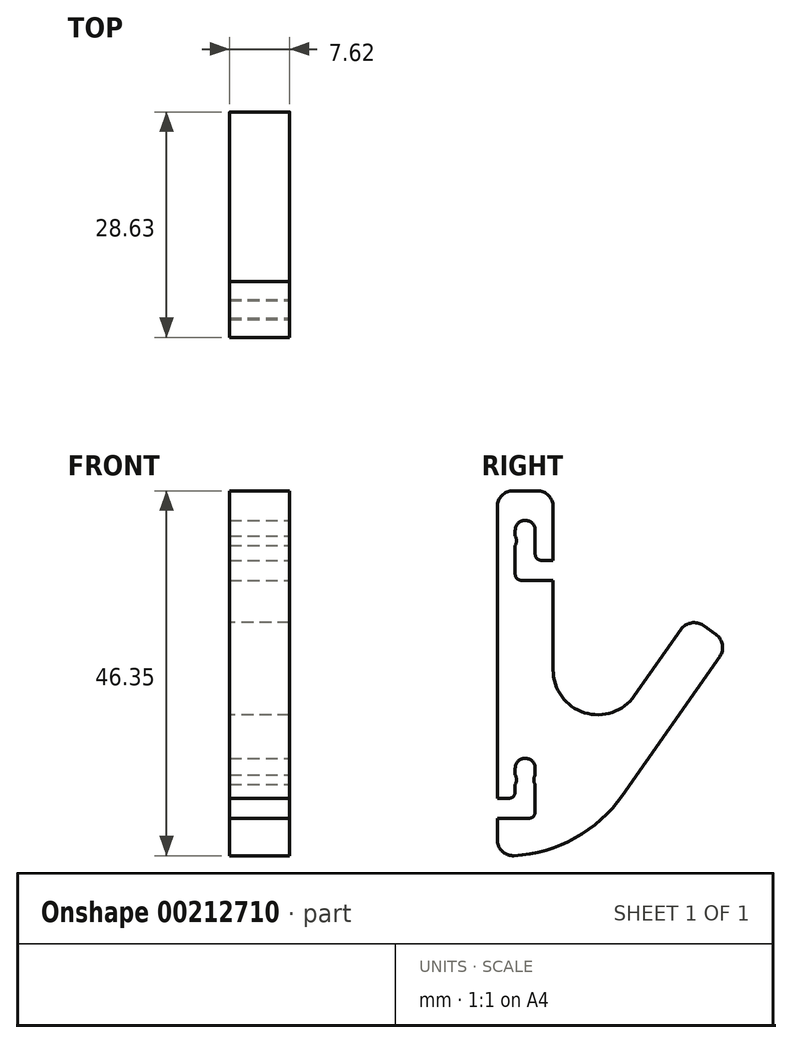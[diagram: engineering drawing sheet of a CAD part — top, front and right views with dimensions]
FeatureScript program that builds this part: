
annotation { "Feature Type Name" : "Feature", "Feature Type Description" : "" }
export const myFeature = defineFeature(function(context is Context, id is Id, definition is map)
    precondition{}
    {
        {
            var Q0;
            Q0=qCreatedBy(makeId("Right.planeOp"),FACE);
            var sketch = newSketch(context, id + "F0", { "sketchPlane" : qUnion([Q0])});
            skLineSegment(sketch, "E0", {"start": v(0, 0) * mm, "end": v(0, 42.36) * mm});
            skLineSegment(sketch, "E1", {"start": v(0, 42.36) * mm, "end": v(7.1, 42.36) * mm});
            skLineSegment(sketch, "E2", {"start": v(7.1, 42.36) * mm, "end": v(7.1, 19.6) * mm});
            skLineSegment(sketch, "E3", {"start": v(29.42, 22.97) * mm, "end": v(24.5, 26.4) * mm});
            skArc(sketch, "E4", {"start": v(7.1, 19.6) * mm, "mid": v(11.08, 14.17) * mm, "end": v(17.45, 16.33) * mm});
            skLineSegment(sketch, "E5", {"start": v(24.5, 26.4) * mm, "end": v(17.45, 16.33) * mm});
            skArc(sketch, "E6", {"start": v(0, -3.98) * mm, "mid": v(8.95, -2.25) * mm, "end": v(15.9, 3.65) * mm});
            skLineSegment(sketch, "E7", {"start": v(29.42, 22.97) * mm, "end": v(15.9, 3.65) * mm});
            skLineSegment(sketch, "E8", {"start": v(0, 0) * mm, "end": v(0, -3.98) * mm});
            skSolve(sketch);
        }
        {
            var Q0;
            Q0=makeQuery(id+"F0.imprint","IMPRINT",FACE,{"disambiguationData":[TD([[makeQuery(id+"F0.imprint","IMPRINT",EDGE,{"derivedFrom":sQuery(id+"F0.wireOp",EDGE,"E0")}),-1.0]])]});
            extrude(context, id + "F1", {"entities" : qUnion([Q0]), "depth" : 7.62 * mm, "symmetric" : true});
        }
        {
            var Q0;
            Q0=makeQuery(id+"F1.opExtrude","SWEPT_EDGE",EDGE,{"disambiguationData":[OSD([sQuery(id+"F0.wireOp",EDGE,"E1"),sQuery(id+"F0.wireOp",EDGE,"E2")])]});
            var Q1;
            Q1=makeQuery(id+"F1.opExtrude","SWEPT_EDGE",EDGE,{"disambiguationData":[OSD([sQuery(id+"F0.wireOp",EDGE,"do6iOSd0-p59h-Iph2-EZYE-FqhHj6ALnol1"),sQuery(id+"F0.wireOp",EDGE,"T0NzOJQf-1ohU-N6pa-0O5Z-Gt8aX7xeZM4e")])]});
            var Q2;
            Q2=makeQuery(id+"F1.opExtrude","SWEPT_EDGE",EDGE,{"disambiguationData":[OSD([sQuery(id+"F0.wireOp",EDGE,"do6iOSd0-p59h-Iph2-EZYE-FqhHj6ALnol1"),sQuery(id+"F0.wireOp",EDGE,"E4")])]});
            var Q3;
            Q3=makeQuery(id+"F1.opExtrude","SWEPT_EDGE",EDGE,{"disambiguationData":[OSD([sQuery(id+"F0.wireOp",EDGE,"do6iOSd0-p59h-Iph2-EZYE-FqhHj6ALnol1"),sQuery(id+"F0.wireOp",EDGE,"T0NzOJQf-1ohU-N6pa-0O5Z-Gt8aX7xeZM4e")])]});
            var Q4;
            Q4=makeQuery(id+"F1.opExtrude","SWEPT_EDGE",EDGE,{"disambiguationData":[OSD([sQuery(id+"F0.wireOp",EDGE,"do6iOSd0-p59h-Iph2-EZYE-FqhHj6ALnol1"),sQuery(id+"F0.wireOp",EDGE,"E4")])]});
            var Q5;
            Q5=makeQuery(id+"F1.opExtrude","SWEPT_EDGE",EDGE,{"disambiguationData":[OSD([sQuery(id+"F0.wireOp",EDGE,"E1"),sQuery(id+"F0.wireOp",EDGE,"917d6a71-8020-47b3-91d0-356564592358.trimOffspring")])]});
            var Q6;
            Q6=makeQuery(id+"F1.opExtrude","SWEPT_EDGE",EDGE,{"disambiguationData":[OSD([sQuery(id+"F0.wireOp",EDGE,"E1"),sQuery(id+"F0.wireOp",EDGE,"E2")])]});
            var Q7;
            Q7=makeQuery(id+"F1.opExtrude","SWEPT_EDGE",EDGE,{"disambiguationData":[OSD([sQuery(id+"F0.wireOp",EDGE,"E1"),sQuery(id+"F0.wireOp",EDGE,"917d6a71-8020-47b3-91d0-356564592358.trimOffspring")])]});
            var Q8;
            Q8=makeQuery(id+"F1.opExtrude","SWEPT_EDGE",EDGE,{"disambiguationData":[OSD([sQuery(id+"F0.wireOp",EDGE,"E1"),sQuery(id+"F0.wireOp",EDGE,"917d6a71-8020-47b3-91d0-356564592358.trimOffspring")])]});
            var Q9;
            Q9=makeQuery(id+"F1.opExtrude","SWEPT_EDGE",EDGE,{"disambiguationData":[OSD([sQuery(id+"F0.wireOp",EDGE,"917d6a71-8020-47b3-91d0-356564592358.trimOffspring"),sQuery(id+"F0.wireOp",EDGE,"oMnLxIvI-c7EB-dOBx-Ktot-nHqWXF2Je9gS")])]});
            var Q10;
            Q10=makeQuery(id+"F1.opExtrude","SWEPT_EDGE",EDGE,{"disambiguationData":[OSD([sQuery(id+"F0.wireOp",EDGE,"E0"),sQuery(id+"F0.wireOp",EDGE,"H5s6PmsO-nB2p-iTXC-beMi-EFhrGGPzX9zd")])]});
            var Q11;
            Q11=makeQuery(id+"F1.opExtrude","SWEPT_EDGE",EDGE,{"disambiguationData":[OSD([sQuery(id+"F0.wireOp",EDGE,"E0"),sQuery(id+"F0.wireOp",EDGE,"H5s6PmsO-nB2p-iTXC-beMi-EFhrGGPzX9zd")])]});
            var Q12;
            Q12=makeQuery(id+"F1.opExtrude","SWEPT_EDGE",EDGE,{"disambiguationData":[OSD([sQuery(id+"F0.wireOp",EDGE,"E0"),sQuery(id+"F0.wireOp",EDGE,"H5s6PmsO-nB2p-iTXC-beMi-EFhrGGPzX9zd")])]});
            var Q13;
            Q13=makeQuery(id+"F1.opExtrude","SWEPT_EDGE",EDGE,{"disambiguationData":[OSD([sQuery(id+"F0.wireOp",EDGE,"E0"),sQuery(id+"F0.wireOp",EDGE,"H5s6PmsO-nB2p-iTXC-beMi-EFhrGGPzX9zd")])]});
            var Q14;
            Q14=makeQuery(id+"F1.opExtrude","SWEPT_EDGE",EDGE,{"disambiguationData":[OSD([sQuery(id+"F0.wireOp",EDGE,"E3"),sQuery(id+"F0.wireOp",EDGE,"E7")])]});
            var Q15;
            Q15=makeQuery(id+"F1.opExtrude","SWEPT_EDGE",EDGE,{"disambiguationData":[OSD([sQuery(id+"F0.wireOp",EDGE,"E3"),sQuery(id+"F0.wireOp",EDGE,"E5")])]});
            var Q16;
            Q16=makeQuery(id+"F1.opExtrude","SWEPT_EDGE",EDGE,{"disambiguationData":[OSD([sQuery(id+"F0.wireOp",EDGE,"E3"),sQuery(id+"F0.wireOp",EDGE,"E5")])]});
            var Q17;
            Q17=makeQuery(id+"F1.opExtrude","SWEPT_EDGE",EDGE,{"disambiguationData":[OSD([sQuery(id+"F0.wireOp",EDGE,"E3"),sQuery(id+"F0.wireOp",EDGE,"E7")])]});
            var Q18;
            Q18=makeQuery(id+"F1.opExtrude","SWEPT_EDGE",EDGE,{"disambiguationData":[OSD([sQuery(id+"F0.wireOp",EDGE,"E3"),sQuery(id+"F0.wireOp",EDGE,"E5")])]});
            var Q19;
            Q19=makeQuery(id+"F1.opExtrude","SWEPT_EDGE",EDGE,{"disambiguationData":[OSD([sQuery(id+"F0.wireOp",EDGE,"E6"),sQuery(id+"F0.wireOp",EDGE,"E8")])]});
            fillet(context, id + "F2", {"entities" : qUnion([Q0, Q1, Q2, Q3, Q4, Q5, Q6, Q7, Q8, Q9, Q10, Q11, Q12, Q13, Q14, Q15, Q16, Q17, Q18, Q19]), "radius" : 2.03 * mm, "tangentPropagation" : true, "allowEdgeOverflow" : false});
        }
        {
            var Q0;
            Q0=makeQuery(id+"F1.opExtrude","CAP_FACE",FACE,{"disambiguationData":[OSD([sQuery(id+"F0.wireOp",EDGE,"E0"),sQuery(id+"F0.wireOp",EDGE,"E1"),sQuery(id+"F0.wireOp",EDGE,"917d6a71-8020-47b3-91d0-356564592358.trimOffspring"),sQuery(id+"F0.wireOp",EDGE,"do6iOSd0-p59h-Iph2-EZYE-FqhHj6ALnol1"),sQuery(id+"F0.wireOp",EDGE,"E2"),sQuery(id+"F0.wireOp",EDGE,"oMnLxIvI-c7EB-dOBx-Ktot-nHqWXF2Je9gS"),sQuery(id+"F0.wireOp",EDGE,"H5s6PmsO-nB2p-iTXC-beMi-EFhrGGPzX9zd"),sQuery(id+"F0.wireOp",EDGE,"E55nDa4c-AnYE-asiw-xueP-FGOoVfwC6I5W"),sQuery(id+"F0.wireOp",EDGE,"E3"),sQuery(id+"F0.wireOp",EDGE,"E4"),sQuery(id+"F0.wireOp",EDGE,"E5"),sQuery(id+"F0.wireOp",EDGE,"E6"),sQuery(id+"F0.wireOp",EDGE,"E7"),sQuery(id+"F0.wireOp",EDGE,"E8"),sQuery(id+"F0.wireOp",EDGE,"yA7TRvCN-UMRo-vrpZ-Ydxq-uWrTOSylFOQI"),sQuery(id+"F0.wireOp",EDGE,"T0NzOJQf-1ohU-N6pa-0O5Z-Gt8aX7xeZM4e"),sQuery(id+"F0.wireOp",EDGE,"pUJUahGI-wT5O-X5Pp-sLFv-ISeCsSa39cJM"),sQuery(id+"F0.wireOp",EDGE,"gnTElwEQ-xExs-yJdp-y54U-xUUldCR7EacK"),sQuery(id+"F0.wireOp",EDGE,"427NVwON-J4Eg-A1F7-4Q2u-34sglIcidLrh")])],"isStart":false});
            var sketch = newSketch(context, id + "F3", { "sketchPlane" : qUnion([Q0])});
            skLineSegment(sketch, "E9", {"start": v(3.55, 37.34) * mm, "end": v(3.55, 21.15) * mm, "construction": true});
            skArc(sketch, "E10", {"start": v(4.82, 37.34) * mm, "mid": v(3.55, 38.61) * mm, "end": v(2.28, 37.34) * mm});
            skLineSegment(sketch, "E11", {"start": v(2.28, 37.34) * mm, "end": v(2.28, 31) * mm});
            skLineSegment(sketch, "E12", {"start": v(2.28, 31) * mm, "end": v(7.1, 31) * mm});
            skLineSegment(sketch, "E13", {"start": v(7.1, 31) * mm, "end": v(7.1, 33.53) * mm});
            skLineSegment(sketch, "E14", {"start": v(7.1, 33.53) * mm, "end": v(4.82, 33.53) * mm});
            skLineSegment(sketch, "E15", {"start": v(4.82, 33.53) * mm, "end": v(4.82, 37.34) * mm});
            skLineSegment(sketch, "E16", {"start": v(3.55, 37.34) * mm, "end": v(3.55, 42.36) * mm, "construction": true});
            skLineSegment(sketch, "E17", {"start": v(0, 21.15) * mm, "end": v(3.55, 21.15) * mm, "construction": true});
            skLineSegment(sketch, "E18", {"start": v(3.55, 21.15) * mm, "end": v(3.55, 7.12) * mm, "construction": true});
            skArc(sketch, "E19", {"start": v(4.82, 7.12) * mm, "mid": v(3.55, 8.39) * mm, "end": v(2.28, 7.12) * mm});
            skLineSegment(sketch, "E20", {"start": v(2.28, 7.12) * mm, "end": v(2.28, 3.3) * mm});
            skLineSegment(sketch, "E21", {"start": v(2.28, 3.3) * mm, "end": v(0, 3.3) * mm});
            skLineSegment(sketch, "E22", {"start": v(0, 3.3) * mm, "end": v(0, 0.77) * mm});
            skLineSegment(sketch, "E23", {"start": v(0, 0.77) * mm, "end": v(4.82, 0.77) * mm});
            skLineSegment(sketch, "E24", {"start": v(4.82, 0.77) * mm, "end": v(4.82, 7.12) * mm});
            skSolve(sketch);
        }
        {
            var Q0;
            Q0 = qSketchRegion(id + "F3", true);
            extrude(context, id + "F4", {"entities" : qUnion([Q0]), "operationType" : NewBodyOperationType.REMOVE, "endBound" : BoundingType.THROUGH_ALL, "oppositeDirection" : true, "depth" : 25.4 * mm});
        }
        {
            var Q0;
            Q0=makeQuery(id+"F4.boolean.opBoolean","COPY",EDGE,{"derivedFrom":makeQuery(id+"F4.opExtrude","SWEPT_EDGE",EDGE,{"disambiguationData":[OSD([sQuery(id+"F3.wireOp",EDGE,"E14"),sQuery(id+"F3.wireOp",EDGE,"E15")])]})});
            var Q1;
            Q1=makeQuery(id+"F4.boolean.opBoolean","COPY",EDGE,{"derivedFrom":makeQuery(id+"F4.opExtrude","SWEPT_EDGE",EDGE,{"disambiguationData":[OSD([sQuery(id+"F0.wireOp",EDGE,"E2"),sQuery(id+"F3.wireOp",EDGE,"E13"),sQuery(id+"F3.wireOp",EDGE,"E14")])]})});
            var Q2;
            Q2=makeQuery(id+"F4.boolean.opBoolean","COPY",EDGE,{"derivedFrom":makeQuery(id+"F4.opExtrude","SWEPT_EDGE",EDGE,{"disambiguationData":[OSD([sQuery(id+"F3.wireOp",EDGE,"E11"),sQuery(id+"F3.wireOp",EDGE,"E12")])]})});
            var Q3;
            Q3=makeQuery(id+"F4.boolean.opBoolean","COPY",EDGE,{"derivedFrom":makeQuery(id+"F4.opExtrude","SWEPT_EDGE",EDGE,{"disambiguationData":[OSD([sQuery(id+"F0.wireOp",EDGE,"E2"),sQuery(id+"F3.wireOp",EDGE,"E12"),sQuery(id+"F3.wireOp",EDGE,"E13")])]})});
            var Q4;
            Q4=makeQuery(id+"F4.boolean.opBoolean","COPY",EDGE,{"derivedFrom":makeQuery(id+"F4.opExtrude","SWEPT_EDGE",EDGE,{"disambiguationData":[OSD([sQuery(id+"F0.wireOp",EDGE,"E0"),sQuery(id+"F0.wireOp",EDGE,"E8"),sQuery(id+"F3.wireOp",EDGE,"E21"),sQuery(id+"F3.wireOp",EDGE,"E22")])]})});
            var Q5;
            Q5=makeQuery(id+"F4.boolean.opBoolean","COPY",EDGE,{"derivedFrom":makeQuery(id+"F4.opExtrude","SWEPT_EDGE",EDGE,{"disambiguationData":[OSD([sQuery(id+"F3.wireOp",EDGE,"E23"),sQuery(id+"F3.wireOp",EDGE,"E24")])]})});
            var Q6;
            Q6=makeQuery(id+"F4.boolean.opBoolean","COPY",EDGE,{"derivedFrom":makeQuery(id+"F4.opExtrude","SWEPT_EDGE",EDGE,{"disambiguationData":[OSD([sQuery(id+"F0.wireOp",EDGE,"E0"),sQuery(id+"F0.wireOp",EDGE,"E8"),sQuery(id+"F3.wireOp",EDGE,"E22"),sQuery(id+"F3.wireOp",EDGE,"E23")])]})});
            var Q7;
            Q7=makeQuery(id+"F4.boolean.opBoolean","COPY",EDGE,{"derivedFrom":makeQuery(id+"F4.opExtrude","SWEPT_EDGE",EDGE,{"disambiguationData":[OSD([sQuery(id+"F3.wireOp",EDGE,"E20"),sQuery(id+"F3.wireOp",EDGE,"E21")])]})});
            fillet(context, id + "F5", {"entities" : qUnion([Q0, Q1, Q2, Q3, Q4, Q5, Q6, Q7]), "radius" : 0.76 * mm, "tangentPropagation" : true, "allowEdgeOverflow" : false});
        }
        {
            var Q0;
            Q0=makeQuery(id+"F1.opExtrude","CAP_FACE",FACE,{"disambiguationData":[OSD([sQuery(id+"F0.wireOp",EDGE,"E0"),sQuery(id+"F0.wireOp",EDGE,"E1"),sQuery(id+"F0.wireOp",EDGE,"E2"),sQuery(id+"F0.wireOp",EDGE,"E3"),sQuery(id+"F0.wireOp",EDGE,"E4"),sQuery(id+"F0.wireOp",EDGE,"E5"),sQuery(id+"F0.wireOp",EDGE,"E6"),sQuery(id+"F0.wireOp",EDGE,"E7"),sQuery(id+"F0.wireOp",EDGE,"E8")])],"isStart":false});
            var sketch = newSketch(context, id + "F6", { "sketchPlane" : qUnion([Q0])});
            skArc(sketch, "E25", {"start": v(2.28, 35.41) * mm, "mid": v(2.45, 36) * mm, "end": v(2.28, 36.6) * mm});
            skCircle(sketch, "E26", {"center": v(3.55, 37.34) * mm, "radius": 1.19 * mm, "construction": true});
            skLineSegment(sketch, "E27", {"start": v(3.55, 37.34) * mm, "end": v(3.55, 20.83) * mm, "construction": true});
            skLineSegment(sketch, "E28", {"start": v(2.28, 35.41) * mm, "end": v(4.82, 35.41) * mm, "construction": true});
            skLineSegment(sketch, "E29", {"start": v(2.28, 36.6) * mm, "end": v(4.82, 36.6) * mm, "construction": true});
            skArc(sketch, "E30.MirrorCS", {"start": v(4.82, 35.41) * mm, "mid": v(4.65, 36) * mm, "end": v(4.82, 36.6) * mm});
            skLineSegment(sketch, "E31", {"start": v(2.28, 36.6) * mm, "end": v(2.28, 35.41) * mm});
            skLineSegment(sketch, "E32.MirrorCS", {"start": v(4.82, 36.6) * mm, "end": v(4.82, 35.41) * mm});
            skLineSegment(sketch, "E33", {"start": v(3.55, 20.83) * mm, "end": v(0, 20.83) * mm, "construction": true});
            skCircle(sketch, "E34", {"center": v(3.55, 7.12) * mm, "radius": 1.19 * mm, "construction": true});
            skLineSegment(sketch, "E35", {"start": v(3.55, 20.83) * mm, "end": v(3.55, 4.32) * mm, "construction": true});
            skLineSegment(sketch, "E36.MirrorCS", {"start": v(2.28, 5.05) * mm, "end": v(2.28, 6.25) * mm});
            skArc(sketch, "E37.MirrorCS", {"start": v(2.28, 6.25) * mm, "mid": v(2.45, 5.65) * mm, "end": v(2.28, 5.05) * mm});
            skArc(sketch, "E38.MirrorCS", {"start": v(4.82, 6.25) * mm, "mid": v(4.65, 5.65) * mm, "end": v(4.82, 5.05) * mm});
            skLineSegment(sketch, "E39.MirrorCS", {"start": v(4.82, 5.05) * mm, "end": v(4.82, 6.25) * mm});
            skSolve(sketch);
        }
        {
            var Q0;
            Q0=makeQuery(id+"F6.imprint","IMPRINT",FACE,{"disambiguationData":[TD([[makeQuery(id+"F6.imprint","IMPRINT",EDGE,{"derivedFrom":sQuery(id+"F6.wireOp",EDGE,"E30.MirrorCS")}),-1.0]])]});
            var Q1;
            Q1=makeQuery(id+"F6.imprint","IMPRINT",FACE,{"disambiguationData":[TD([[makeQuery(id+"F6.imprint","IMPRINT",EDGE,{"derivedFrom":sQuery(id+"F6.wireOp",EDGE,"E25")}),1.0]])]});
            var Q2;
            Q2=makeQuery(id+"F6.imprint","IMPRINT",FACE,{"disambiguationData":[TD([[makeQuery(id+"F6.imprint","IMPRINT",EDGE,{"derivedFrom":sQuery(id+"F6.wireOp",EDGE,"E36.MirrorCS")}),1.0]])]});
            var Q3;
            Q3=makeQuery(id+"F6.imprint","IMPRINT",FACE,{"disambiguationData":[TD([[makeQuery(id+"F6.imprint","IMPRINT",EDGE,{"derivedFrom":sQuery(id+"F6.wireOp",EDGE,"E38.MirrorCS")}),1.0]])]});
            var Q4;
            Q4=makeQuery(id+"F1.opExtrude","CAP_FACE",FACE,{"disambiguationData":[OSD([sQuery(id+"F0.wireOp",EDGE,"E0"),sQuery(id+"F0.wireOp",EDGE,"E1"),sQuery(id+"F0.wireOp",EDGE,"E2"),sQuery(id+"F0.wireOp",EDGE,"E3"),sQuery(id+"F0.wireOp",EDGE,"E4"),sQuery(id+"F0.wireOp",EDGE,"E5"),sQuery(id+"F0.wireOp",EDGE,"E6"),sQuery(id+"F0.wireOp",EDGE,"E7"),sQuery(id+"F0.wireOp",EDGE,"E8")])],"isStart":true});
            extrude(context, id + "F7", {"entities" : qUnion([Q0, Q1, Q2, Q3]), "operationType" : NewBodyOperationType.ADD, "endBound" : BoundingType.UP_TO_SURFACE, "oppositeDirection" : true, "endBoundEntityFace" : qUnion([Q4]), "depth" : 25.4 * mm});
        }
    });
